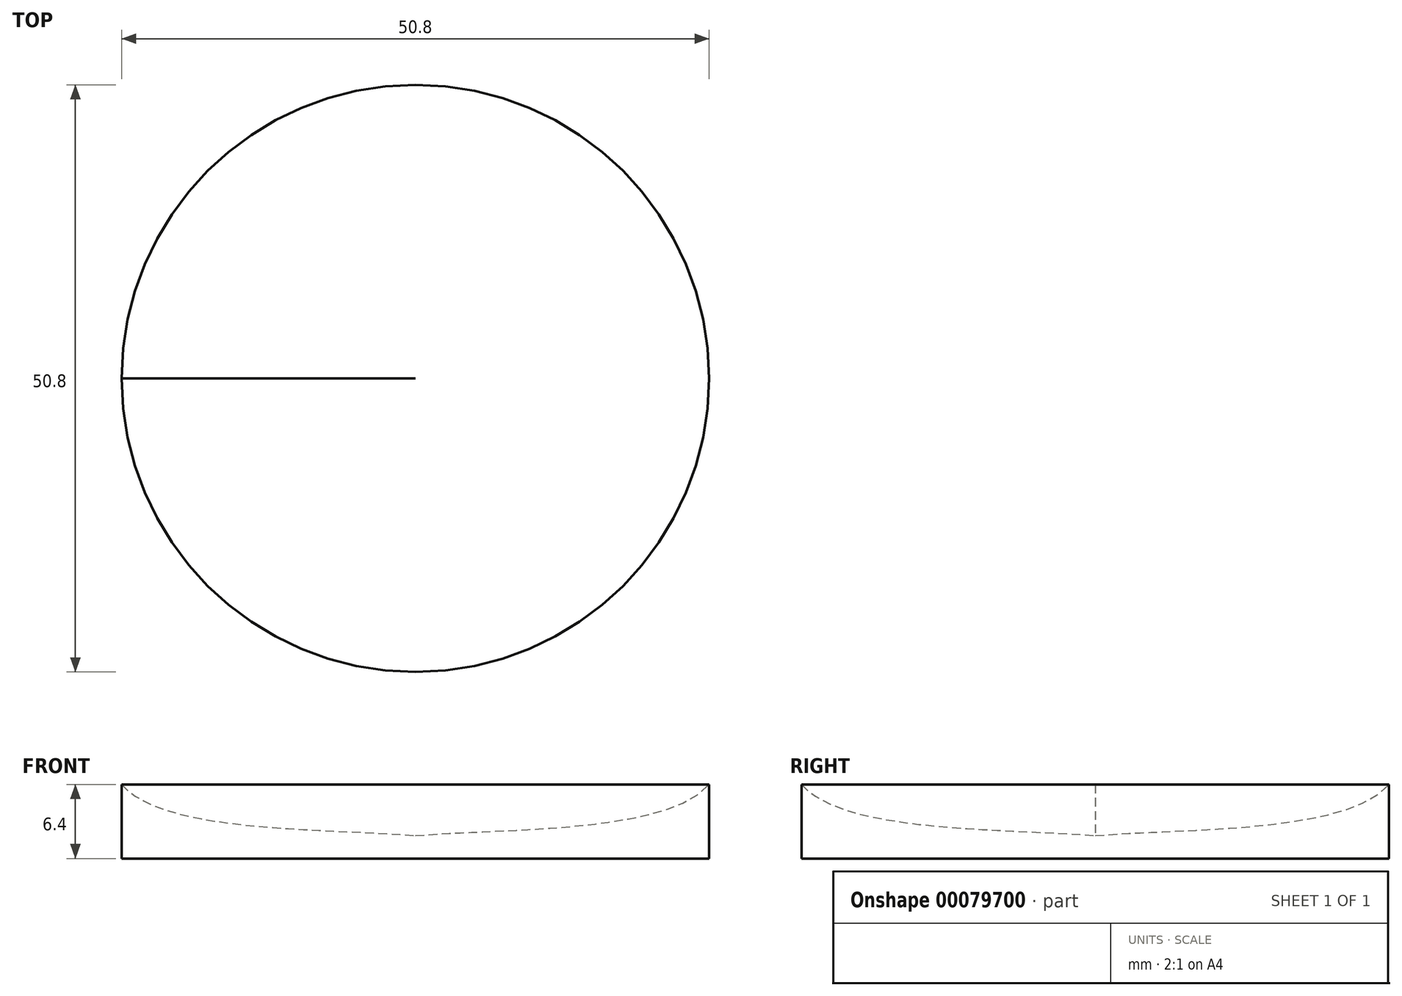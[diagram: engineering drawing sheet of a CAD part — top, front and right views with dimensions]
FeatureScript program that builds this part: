
annotation { "Feature Type Name" : "Feature", "Feature Type Description" : "" }
export const myFeature = defineFeature(function(context is Context, id is Id, definition is map)
    precondition{}
    {
        {
            var Q0;
            Q0=qCreatedBy(makeId("Front.planeOp"),FACE);
            var sketch = newSketch(context, id + "F0", { "sketchPlane" : qUnion([Q0])});
            skLineSegment(sketch, "E0", {"start": v(0, 0) * mm, "end": v(-25.4, 0) * mm});
            skLineSegment(sketch, "E1", {"start": v(-25.4, 0) * mm, "end": v(-25.4, 6.4) * mm});
            skLineSegment(sketch, "E2", {"start": v(0, 0) * mm, "end": v(0, 1.98) * mm});
            skFitSpline(sketch, "E3", {"points": [v(-25.4, 6.4) * mm, v(0, 1.98) * mm], "startDerivative": vector(11, -12.7) * mm, "endDerivative": vector(23.42, -1.98) * mm});
            skSolve(sketch);
        }
        {
            var Q0;
            Q0=makeQuery(id+"F0.imprint","IMPRINT",FACE,{"disambiguationData":[TD([[makeQuery(id+"F0.imprint","IMPRINT",EDGE,{"derivedFrom":sQuery(id+"F0.wireOp",EDGE,"E0")}),-1.0]])]});
            var Q1;
            Q1=sQuery(id+"F0.wireOp",EDGE,"E2");
            revolve(context, id + "F1", {"entities" : qUnion([Q0]), "axis" : qUnion([Q1]), "revolveType" : RevolveType.FULL});
        }
    });
